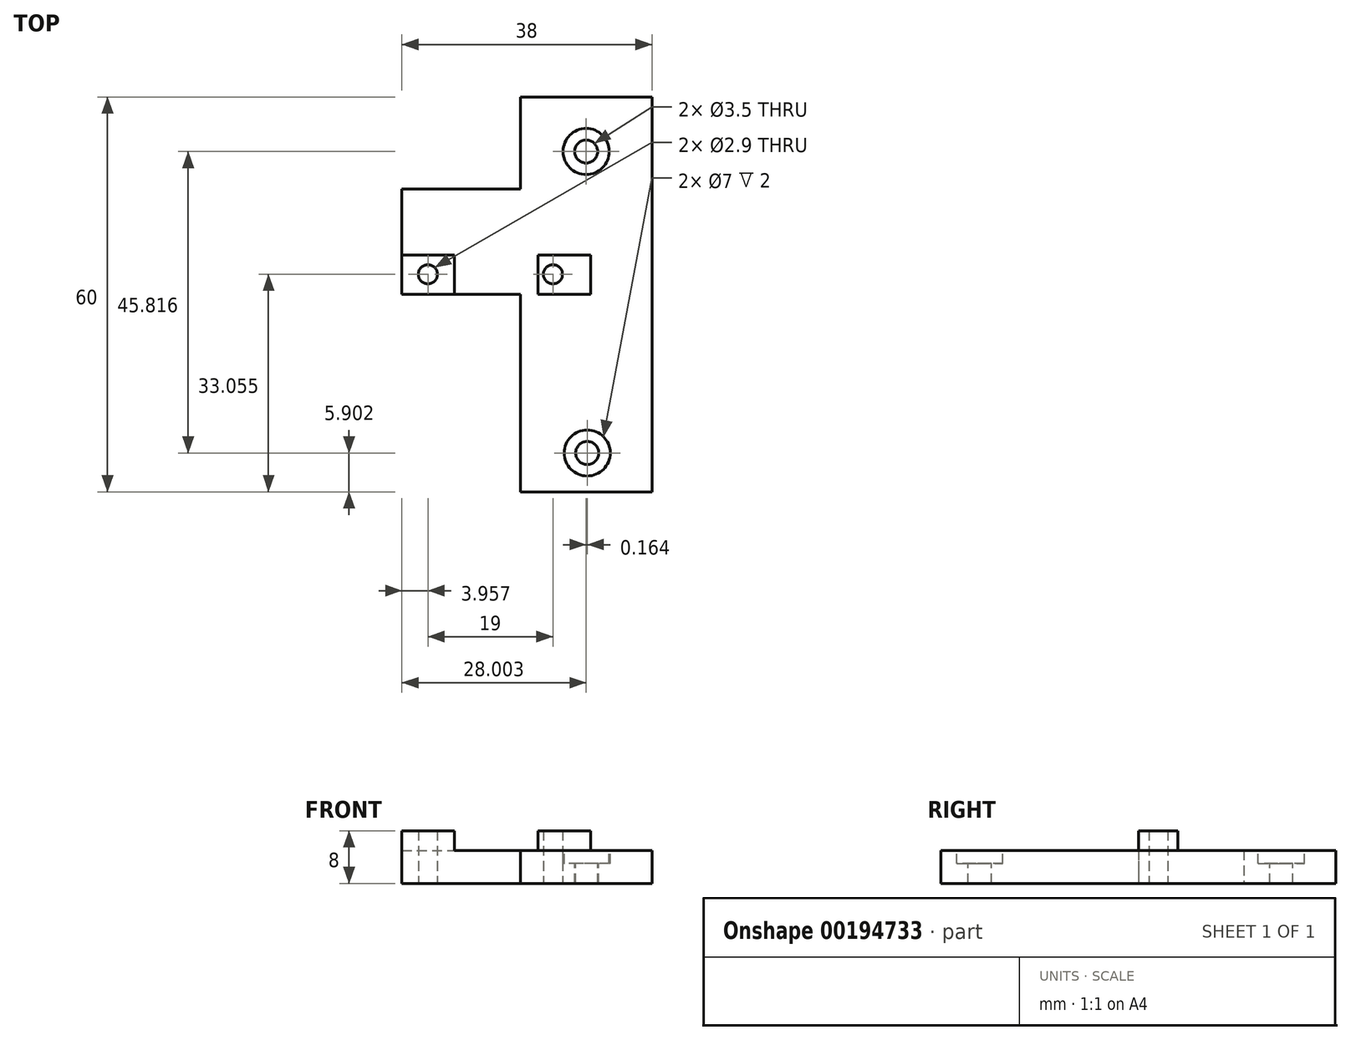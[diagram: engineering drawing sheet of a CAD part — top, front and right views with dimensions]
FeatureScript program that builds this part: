
annotation { "Feature Type Name" : "Feature", "Feature Type Description" : "" }
export const myFeature = defineFeature(function(context is Context, id is Id, definition is map)
    precondition{}
    {
        {
            var Q0;
            Q0=qCreatedBy(makeId("Top.planeOp"),FACE);
            var sketch = newSketch(context, id + "F0", { "sketchPlane" : qUnion([Q0])});
            skLineSegment(sketch, "E0", {"start": v(0, 0) * mm, "end": v(0, 30) * mm});
            skLineSegment(sketch, "E1", {"start": v(0, 30) * mm, "end": v(-18, 30) * mm});
            skLineSegment(sketch, "E2", {"start": v(-18, 30) * mm, "end": v(-18, 46) * mm});
            skLineSegment(sketch, "E3", {"start": v(-18, 46) * mm, "end": v(0, 46) * mm});
            skLineSegment(sketch, "E4", {"start": v(0, 46) * mm, "end": v(0, 60) * mm});
            skLineSegment(sketch, "E5", {"start": v(0, 60) * mm, "end": v(20, 60) * mm});
            skLineSegment(sketch, "E6", {"start": v(20, 60) * mm, "end": v(20, 0) * mm});
            skLineSegment(sketch, "E7", {"start": v(20, 0) * mm, "end": v(0, 0) * mm});
            skCircle(sketch, "E8", {"center": v(-14.04, 33.06) * mm, "radius": 1.45 * mm});
            skCircle(sketch, "E9", {"center": v(4.96, 33.06) * mm, "radius": 1.45 * mm});
            skSolve(sketch);
        }
        {
            var Q0;
            Q0=makeQuery(id+"F0.imprint","IMPRINT",FACE,{"disambiguationData":[TD([[makeQuery(id+"F0.imprint","IMPRINT",EDGE,{"derivedFrom":sQuery(id+"F0.wireOp",EDGE,"E0")}),-1.0]])]});
            extrude(context, id + "F1", {"entities" : qUnion([Q0]), "depth" : 5 * mm});
        }
        {
            var Q0;
            Q0=makeQuery(id+"F1.opExtrude","CAP_FACE",FACE,{"disambiguationData":[OSD([sQuery(id+"F0.wireOp",EDGE,"E0"),sQuery(id+"F0.wireOp",EDGE,"E1"),sQuery(id+"F0.wireOp",EDGE,"E2"),sQuery(id+"F0.wireOp",EDGE,"E3"),sQuery(id+"F0.wireOp",EDGE,"E4"),sQuery(id+"F0.wireOp",EDGE,"E5"),sQuery(id+"F0.wireOp",EDGE,"E6"),sQuery(id+"F0.wireOp",EDGE,"E7"),sQuery(id+"F0.wireOp",EDGE,"E8"),sQuery(id+"F0.wireOp",EDGE,"E9")])],"isStart":false});
            var sketch = newSketch(context, id + "F2", { "sketchPlane" : qUnion([Q0])});
            skPoint(sketch, "E10.endSnap0", {"position": v(10, 60) * mm});
            skCircle(sketch, "E11", {"center": v(10, 51.72) * mm, "radius": 1.75 * mm});
            skCircle(sketch, "E12", {"center": v(10.17, 5.9) * mm, "radius": 1.75 * mm});
            skSolve(sketch);
        }
        {
            var Q0;
            Q0=makeQuery(id+"F2.imprint","IMPRINT",FACE,{"disambiguationData":[TD([[makeQuery(id+"F2.imprint","IMPRINT",EDGE,{"derivedFrom":sQuery(id+"F2.wireOp",EDGE,"E11")}),1.0]])]});
            var Q1;
            Q1=makeQuery(id+"F2.imprint","IMPRINT",FACE,{"disambiguationData":[TD([[makeQuery(id+"F2.imprint","IMPRINT",EDGE,{"derivedFrom":sQuery(id+"F2.wireOp",EDGE,"E12")}),1.0]])]});
            var Q2;
            Q2=sQuery(id+"F2.wireOp",EDGE,"E11");
            var Q3;
            Q3=sQuery(id+"F2.wireOp",EDGE,"E12");
            extrude(context, id + "F3", {"entities" : qUnion([Q0, Q1]), "operationType" : NewBodyOperationType.REMOVE, "surfaceEntities" : qUnion([Q2, Q3]), "oppositeDirection" : true, "depth" : 25 * mm});
        }
        {
            var Q0;
            Q0=makeQuery(id+"F1.opExtrude","CAP_FACE",FACE,{"disambiguationData":[OSD([sQuery(id+"F0.wireOp",EDGE,"E0"),sQuery(id+"F0.wireOp",EDGE,"E1"),sQuery(id+"F0.wireOp",EDGE,"E2"),sQuery(id+"F0.wireOp",EDGE,"E3"),sQuery(id+"F0.wireOp",EDGE,"E4"),sQuery(id+"F0.wireOp",EDGE,"E5"),sQuery(id+"F0.wireOp",EDGE,"E6"),sQuery(id+"F0.wireOp",EDGE,"E7"),sQuery(id+"F0.wireOp",EDGE,"E8"),sQuery(id+"F0.wireOp",EDGE,"E9")])],"isStart":false});
            var sketch = newSketch(context, id + "F4", { "sketchPlane" : qUnion([Q0])});
            skLineSegment(sketch, "E13.bottom", {"start": v(-18, 30) * mm, "end": v(-10, 30) * mm});
            skLineSegment(sketch, "E13.top", {"start": v(-18, 36) * mm, "end": v(-10, 36) * mm});
            skLineSegment(sketch, "E13.left", {"start": v(-18, 30) * mm, "end": v(-18, 36) * mm});
            skLineSegment(sketch, "E13.right", {"start": v(-10, 30) * mm, "end": v(-10, 36) * mm});
            skLineSegment(sketch, "E14.bottom", {"start": v(2.68, 30) * mm, "end": v(10.68, 30) * mm});
            skLineSegment(sketch, "E14.top", {"start": v(2.68, 36) * mm, "end": v(10.68, 36) * mm});
            skLineSegment(sketch, "E14.left", {"start": v(2.68, 30) * mm, "end": v(2.68, 36) * mm});
            skLineSegment(sketch, "E14.right", {"start": v(10.68, 30) * mm, "end": v(10.68, 36) * mm});
            skCircle(sketch, "E15", {"center": v(-14.04, 33.06) * mm, "radius": 1.4 * mm});
            skCircle(sketch, "E16", {"center": v(4.96, 33.06) * mm, "radius": 1.4 * mm});
            skSolve(sketch);
        }
        {
            var Q0;
            Q0=makeQuery(id+"F4.imprint","IMPRINT",FACE,{"disambiguationData":[TD([[makeQuery(id+"F4.imprint","IMPRINT",EDGE,{"derivedFrom":sQuery(id+"F4.wireOp",EDGE,"E13.bottom")}),-1.0]])]});
            var Q1;
            Q1=makeQuery(id+"F4.imprint","IMPRINT",FACE,{"disambiguationData":[TD([[makeQuery(id+"F4.imprint","IMPRINT",EDGE,{"derivedFrom":sQuery(id+"F4.wireOp",EDGE,"E14.bottom")}),1.0]])]});
            extrude(context, id + "F5", {"entities" : qUnion([Q0, Q1]), "operationType" : NewBodyOperationType.ADD, "depth" : 3 * mm});
        }
        {
            var Q0;
            Q0=makeQuery(id+"F1.opExtrude","CAP_FACE",FACE,{"disambiguationData":[OSD([sQuery(id+"F0.wireOp",EDGE,"E0"),sQuery(id+"F0.wireOp",EDGE,"E1"),sQuery(id+"F0.wireOp",EDGE,"E2"),sQuery(id+"F0.wireOp",EDGE,"E3"),sQuery(id+"F0.wireOp",EDGE,"E4"),sQuery(id+"F0.wireOp",EDGE,"E5"),sQuery(id+"F0.wireOp",EDGE,"E6"),sQuery(id+"F0.wireOp",EDGE,"E7"),sQuery(id+"F0.wireOp",EDGE,"E8"),sQuery(id+"F0.wireOp",EDGE,"E9")])],"isStart":false});
            var sketch = newSketch(context, id + "F6", { "sketchPlane" : qUnion([Q0])});
            skCircle(sketch, "E17", {"center": v(10, 51.72) * mm, "radius": 3.5 * mm});
            skCircle(sketch, "E18", {"center": v(10.17, 5.9) * mm, "radius": 3.5 * mm});
            skSolve(sketch);
        }
        {
            var Q0;
            Q0 = qSketchRegion(id + "F6", true);
            extrude(context, id + "F7", {"entities" : qUnion([Q0]), "operationType" : NewBodyOperationType.REMOVE, "oppositeDirection" : true, "depth" : 2 * mm});
        }
    });
